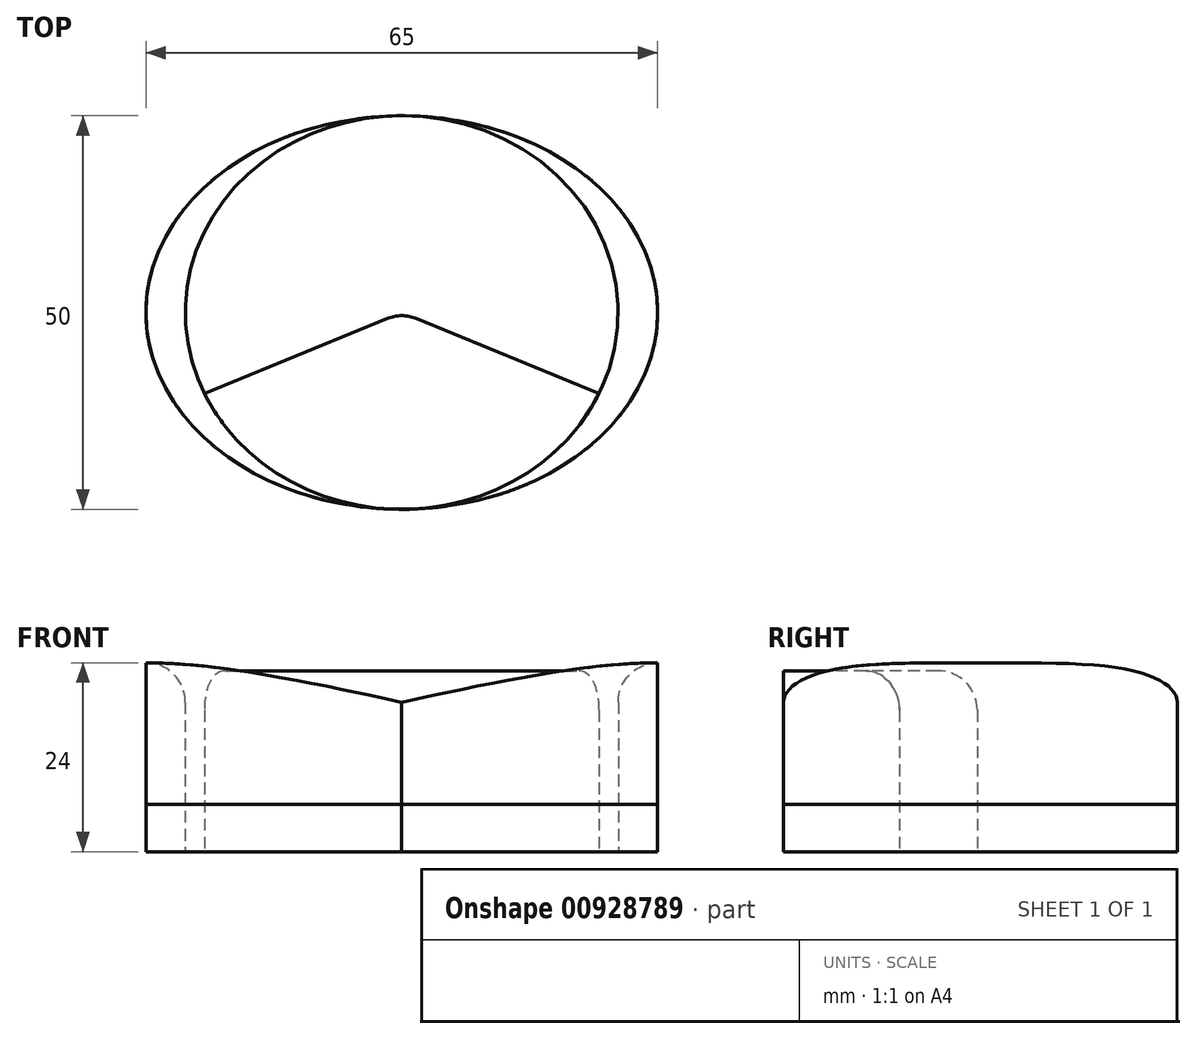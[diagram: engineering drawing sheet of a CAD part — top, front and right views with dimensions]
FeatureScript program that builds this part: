
annotation { "Feature Type Name" : "Feature", "Feature Type Description" : "" }
export const myFeature = defineFeature(function(context is Context, id is Id, definition is map)
    precondition{}
    {
        {
            var Q0;
            Q0=qCreatedBy(makeId("Top.planeOp"),FACE);
            var sketch = newSketch(context, id + "F0", { "sketchPlane" : qUnion([Q0])});
            skEllipse(sketch, "E0", {"center": v(0, 0) * mm, "majorRadius": 32.5 * mm, "minorRadius": 25 * mm, "majorAxis": v(1, 0)});
            skLineSegment(sketch, "E1", {"start": v(-28.69, -11.75) * mm, "end": v(0, 0) * mm});
            skLineSegment(sketch, "E2", {"start": v(0, 0) * mm, "end": v(28.69, -11.75) * mm});
            skEllipse(sketch, "E3", {"center": v(0, 0) * mm, "majorRadius": 27.5 * mm, "minorRadius": 25 * mm, "majorAxis": v(1, 0)});
            skSolve(sketch);
        }
        {
            var Q0;
            {var subQ0=sQuery(id+"F0.wireOp",EDGE,"E2");var subQ1=sQuery(id+"F0.wireOp",EDGE,"E0");var subQ2=makeQuery(id+"F0.imprint","INTERSECT",VERTEX,{"derivedFrom":[subQ1,subQ0]});Q0=makeQuery(id+"F0.imprint","IMPRINT",FACE,{"disambiguationData":[TD([[makeQuery(id+"F0.imprint","IMPRINT",EDGE,{"disambiguationData":[TD([[subQ2,-1.0]])],"derivedFrom":subQ1}),1.0]])]});}
            var Q1;
            {var subQ0=sQuery(id+"F0.wireOp",EDGE,"E1");var subQ1=sQuery(id+"F0.wireOp",EDGE,"E0");var subQ2=makeQuery(id+"F0.imprint","INTERSECT",VERTEX,{"derivedFrom":[subQ1,subQ0]});Q1=makeQuery(id+"F0.imprint","IMPRINT",FACE,{"disambiguationData":[TD([[makeQuery(id+"F0.imprint","IMPRINT",EDGE,{"disambiguationData":[TD([[subQ2,1.0]])],"derivedFrom":subQ1}),1.0]])]});}
            var Q2;
            {var subQ0=sQuery(id+"F0.wireOp",EDGE,"E2");var subQ1=sQuery(id+"F0.wireOp",EDGE,"E0");var subQ2=makeQuery(id+"F0.imprint","INTERSECT",VERTEX,{"derivedFrom":[subQ1,subQ0]});Q2=makeQuery(id+"F0.imprint","IMPRINT",FACE,{"disambiguationData":[TD([[makeQuery(id+"F0.imprint","IMPRINT",EDGE,{"disambiguationData":[TD([[subQ2,1.0]])],"derivedFrom":subQ1}),1.0]])]});}
            var Q3;
            {var subQ0=sQuery(id+"F0.wireOp",EDGE,"E1");var subQ1=sQuery(id+"F0.wireOp",EDGE,"E0");var subQ2=makeQuery(id+"F0.imprint","INTERSECT",VERTEX,{"derivedFrom":[subQ1,subQ0]});Q3=makeQuery(id+"F0.imprint","IMPRINT",FACE,{"disambiguationData":[TD([[makeQuery(id+"F0.imprint","IMPRINT",EDGE,{"disambiguationData":[TD([[subQ2,-1.0]])],"derivedFrom":subQ1}),1.0]])]});}
            extrude(context, id + "F1", {"entities" : qUnion([Q0, Q1, Q2, Q3]), "depth" : 24 * mm, "offsetDistance" : 25 * mm});
        }
        {
            var Q0;
            {var subQ0=sQuery(id+"F0.wireOp",EDGE,"E2");var subQ1=sQuery(id+"F0.wireOp",EDGE,"E1");var subQ2=makeQuery(id+"F0.imprint","INTERSECT",VERTEX,{"derivedFrom":[subQ1,subQ0]});Q0=makeQuery(id+"F0.imprint","IMPRINT",FACE,{"disambiguationData":[TD([[makeQuery(id+"F0.imprint","IMPRINT",EDGE,{"disambiguationData":[TD([[subQ2,1.0]])],"derivedFrom":subQ1}),-1.0]])]});}
            extrude(context, id + "F2", {"entities" : qUnion([Q0]), "depth" : 23 * mm, "offsetDistance" : 25 * mm});
        }
        {
            var Q0;
            Q0 = qSketchRegion(id + "F0", true);
            extrude(context, id + "F3", {"entities" : qUnion([Q0]), "depth" : 6 * mm, "offsetDistance" : 25 * mm});
        }
        {
            var Q0;
            Q0=makeQuery(id+"F2.opExtrude","SWEPT_EDGE",EDGE,{"disambiguationData":[OSD([sQuery(id+"F0.wireOp",EDGE,"E1"),sQuery(id+"F0.wireOp",EDGE,"E2")])]});
            var Q1;
            {var subQ0=sQuery(id+"F0.wireOp",EDGE,"E3");var subQ1=sQuery(id+"F0.wireOp",EDGE,"E0");Q1=makeQuery(id+"F1.opExtrude","CAP_EDGE",EDGE,{"disambiguationData":[OSD([subQ0]),TDD([makeQuery(id+"F0.imprint","IMPRINT",EDGE,{"disambiguationData":[TD([[makeQuery(id+"F0.imprint","INTERSECT",VERTEX,{"disambiguationData":[OD(1.0)],"derivedFrom":[subQ1,subQ0]}),-1.0]])],"derivedFrom":subQ0}),makeQuery(id+"F0.imprint","IMPRINT",EDGE,{"disambiguationData":[TD([[makeQuery(id+"F0.imprint","INTERSECT",VERTEX,{"disambiguationData":[OD(0.0)],"derivedFrom":[subQ1,subQ0]}),1.0]])],"derivedFrom":subQ0})])],"isStart":false});}
            var Q2;
            {var subQ0=sQuery(id+"F0.wireOp",EDGE,"E3");var subQ1=sQuery(id+"F0.wireOp",EDGE,"E0");Q2=makeQuery(id+"F1.opExtrude","CAP_EDGE",EDGE,{"disambiguationData":[OSD([subQ0]),TDD([makeQuery(id+"F0.imprint","IMPRINT",EDGE,{"disambiguationData":[TD([[makeQuery(id+"F0.imprint","INTERSECT",VERTEX,{"disambiguationData":[OD(0.0)],"derivedFrom":[subQ1,subQ0]}),-1.0]])],"derivedFrom":subQ0}),makeQuery(id+"F0.imprint","IMPRINT",EDGE,{"disambiguationData":[TD([[makeQuery(id+"F0.imprint","INTERSECT",VERTEX,{"disambiguationData":[OD(1.0)],"derivedFrom":[subQ1,subQ0]}),1.0]])],"derivedFrom":subQ0})])],"isStart":false});}
            var Q3;
            Q3=makeQuery(id+"F2.opExtrude","CAP_EDGE",EDGE,{"disambiguationData":[OSD([sQuery(id+"F0.wireOp",EDGE,"E2")])],"isStart":false});
            var Q4;
            Q4=makeQuery(id+"F2.opExtrude","CAP_EDGE",EDGE,{"disambiguationData":[OSD([sQuery(id+"F0.wireOp",EDGE,"E1")])],"isStart":false});
            fillet(context, id + "F4", {"entities" : qUnion([Q0, Q1, Q2, Q3, Q4]), "radius" : 5 * mm, "tangentPropagation" : true, "allowEdgeOverflow" : false});
        }
    });
